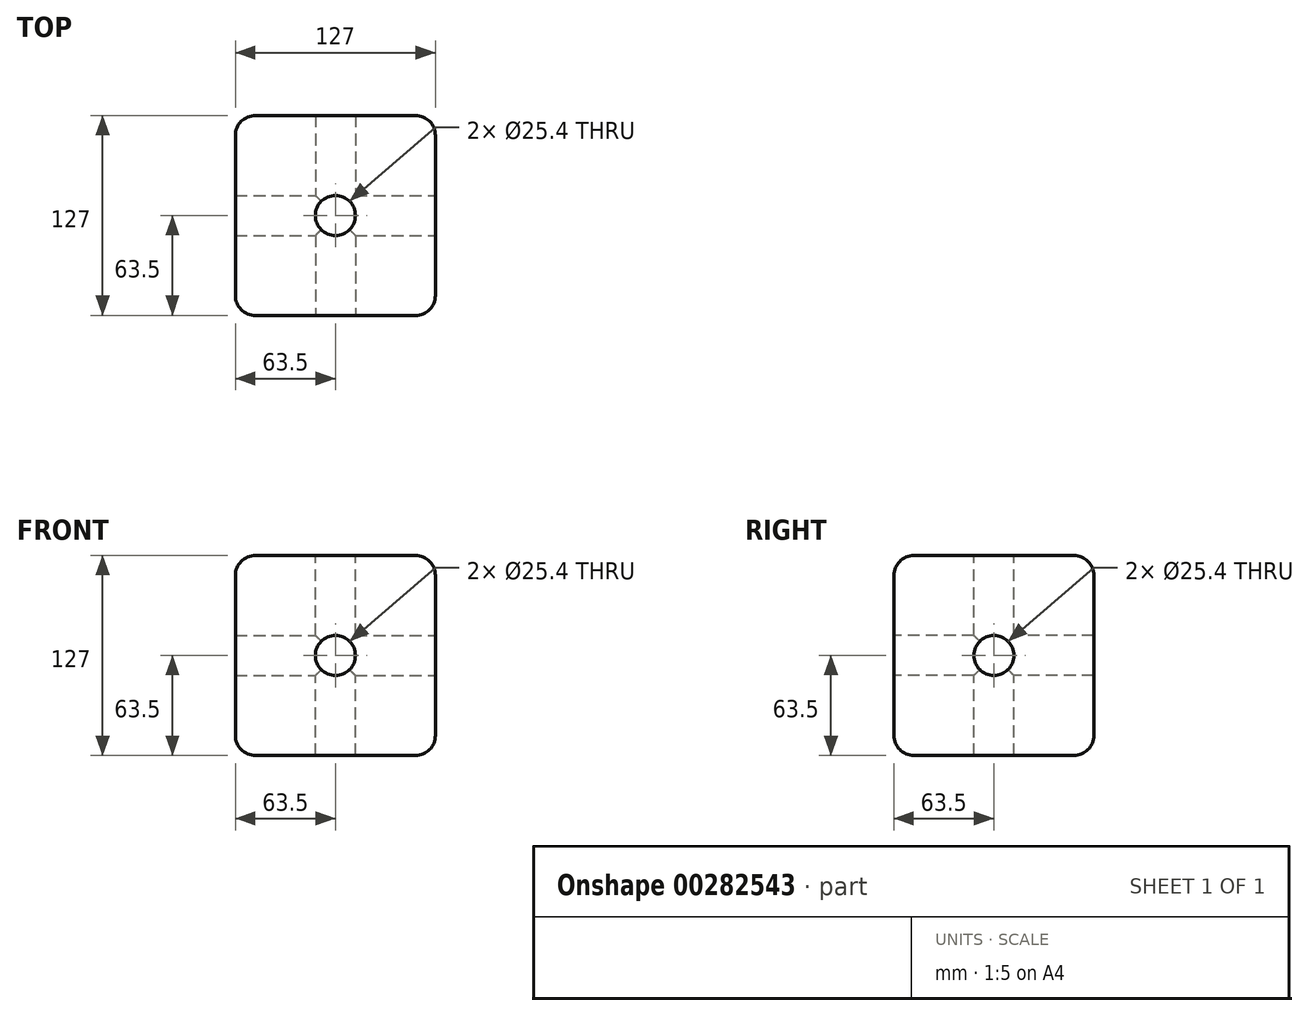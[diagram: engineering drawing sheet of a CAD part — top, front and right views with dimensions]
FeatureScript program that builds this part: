
annotation { "Feature Type Name" : "Feature", "Feature Type Description" : "" }
export const myFeature = defineFeature(function(context is Context, id is Id, definition is map)
    precondition{}
    {
        {
            var Q0;
            Q0=qCreatedBy(makeId("Top.planeOp"),FACE);
            var sketch = newSketch(context, id + "F0", { "sketchPlane" : qUnion([Q0])});
            skLineSegment(sketch, "E0.bottom", {"start": v(63.5, 63.5) * mm, "end": v(-63.5, 63.5) * mm});
            skLineSegment(sketch, "E0.top", {"start": v(63.5, -63.5) * mm, "end": v(-63.5, -63.5) * mm});
            skLineSegment(sketch, "E0.left", {"start": v(63.5, 63.5) * mm, "end": v(63.5, -63.5) * mm});
            skLineSegment(sketch, "E0.right", {"start": v(-63.5, 63.5) * mm, "end": v(-63.5, -63.5) * mm});
            skPoint(sketch, "E0.middle", {"position": v(0, 0) * mm});
            skSolve(sketch);
        }
        {
            var Q0;
            Q0=makeQuery(id+"F0.imprint","IMPRINT",FACE,{"disambiguationData":[TD([[makeQuery(id+"F0.imprint","IMPRINT",EDGE,{"derivedFrom":sQuery(id+"F0.wireOp",EDGE,"E0.bottom")}),1.0]])]});
            extrude(context, id + "F1", {"entities" : qUnion([Q0]), "depth" : 63.5 * mm});
        }
        {
            var Q0;
            Q0=makeQuery(id+"F1.opExtrude","CAP_FACE",FACE,{"disambiguationData":[OSD([sQuery(id+"F0.wireOp",EDGE,"E0.bottom"),sQuery(id+"F0.wireOp",EDGE,"E0.top"),sQuery(id+"F0.wireOp",EDGE,"E0.left"),sQuery(id+"F0.wireOp",EDGE,"E0.right")])],"isStart":true});
            var Q1;
            Q1=makeQuery(id+"F1.opExtrude","CAP_FACE",FACE,{"disambiguationData":[OSD([sQuery(id+"F0.wireOp",EDGE,"E0.bottom"),sQuery(id+"F0.wireOp",EDGE,"E0.top"),sQuery(id+"F0.wireOp",EDGE,"E0.left"),sQuery(id+"F0.wireOp",EDGE,"E0.right")])],"isStart":false});
            extrude(context, id + "F2", {"entities" : qUnion([Q0, Q1]), "operationType" : NewBodyOperationType.ADD, "depth" : 63.5 * mm});
        }
        {
            var Q0;
            Q0=makeQuery(id+"F1.opExtrude","CAP_EDGE",EDGE,{"disambiguationData":[OSD([sQuery(id+"F0.wireOp",EDGE,"E0.top")])],"isStart":false});
            var Q1;
            Q1=makeQuery(id+"F1.opExtrude","CAP_EDGE",EDGE,{"disambiguationData":[OSD([sQuery(id+"F0.wireOp",EDGE,"E0.right")])],"isStart":false});
            var Q2;
            {var subQ0=sQuery(id+"F0.wireOp",EDGE,"E0.right");var subQ1=sQuery(id+"F0.wireOp",EDGE,"E0.top");Q2=makeQuery(id+"F2.boolean.opBoolean","MERGE",EDGE,{"derivedFrom":[makeQuery(id+"F1.opExtrude","SWEPT_EDGE",EDGE,{"disambiguationData":[OSD([subQ1,subQ0])]}),makeQuery(id+"F2.opExtrude","SWEPT_EDGE",EDGE,{"disambiguationData":[OSD([subQ1,subQ0]),TDD([makeQuery(id+"F1.opExtrude","CAP_VERTEX",VERTEX,{"disambiguationData":[OSD([subQ1,subQ0])],"isStart":true})])]}),makeQuery(id+"F2.opExtrude","SWEPT_EDGE",EDGE,{"disambiguationData":[OSD([subQ1,subQ0]),TDD([makeQuery(id+"F1.opExtrude","CAP_VERTEX",VERTEX,{"disambiguationData":[OSD([subQ1,subQ0])],"isStart":false})])]})]});}
            var Q3;
            Q3=makeQuery(id+"F1.opExtrude","CAP_EDGE",EDGE,{"disambiguationData":[OSD([sQuery(id+"F0.wireOp",EDGE,"E0.bottom")])],"isStart":false});
            var Q4;
            Q4=makeQuery(id+"F1.opExtrude","CAP_EDGE",EDGE,{"disambiguationData":[OSD([sQuery(id+"F0.wireOp",EDGE,"E0.left")])],"isStart":false});
            var Q5;
            {var subQ0=sQuery(id+"F0.wireOp",EDGE,"E0.left");var subQ1=sQuery(id+"F0.wireOp",EDGE,"E0.bottom");Q5=makeQuery(id+"F2.boolean.opBoolean","MERGE",EDGE,{"derivedFrom":[makeQuery(id+"F1.opExtrude","SWEPT_EDGE",EDGE,{"disambiguationData":[OSD([subQ1,subQ0])]}),makeQuery(id+"F2.opExtrude","SWEPT_EDGE",EDGE,{"disambiguationData":[OSD([subQ1,subQ0]),TDD([makeQuery(id+"F1.opExtrude","CAP_VERTEX",VERTEX,{"disambiguationData":[OSD([subQ1,subQ0])],"isStart":true})])]}),makeQuery(id+"F2.opExtrude","SWEPT_EDGE",EDGE,{"disambiguationData":[OSD([subQ1,subQ0]),TDD([makeQuery(id+"F1.opExtrude","CAP_VERTEX",VERTEX,{"disambiguationData":[OSD([subQ1,subQ0])],"isStart":false})])]})]});}
            var Q6;
            {var subQ0=sQuery(id+"F0.wireOp",EDGE,"E0.left");var subQ1=sQuery(id+"F0.wireOp",EDGE,"E0.top");Q6=makeQuery(id+"F2.boolean.opBoolean","MERGE",EDGE,{"derivedFrom":[makeQuery(id+"F1.opExtrude","SWEPT_EDGE",EDGE,{"disambiguationData":[OSD([subQ1,subQ0])]}),makeQuery(id+"F2.opExtrude","SWEPT_EDGE",EDGE,{"disambiguationData":[OSD([subQ1,subQ0]),TDD([makeQuery(id+"F1.opExtrude","CAP_VERTEX",VERTEX,{"disambiguationData":[OSD([subQ1,subQ0])],"isStart":true})])]}),makeQuery(id+"F2.opExtrude","SWEPT_EDGE",EDGE,{"disambiguationData":[OSD([subQ1,subQ0]),TDD([makeQuery(id+"F1.opExtrude","CAP_VERTEX",VERTEX,{"disambiguationData":[OSD([subQ1,subQ0])],"isStart":false})])]})]});}
            var Q7;
            {var subQ0=sQuery(id+"F0.wireOp",EDGE,"E0.left");Q7=makeQuery(id+"F2.opExtrude","CAP_EDGE",EDGE,{"disambiguationData":[OSD([subQ0]),TDD([makeQuery(id+"F1.opExtrude","CAP_EDGE",EDGE,{"disambiguationData":[OSD([subQ0])],"isStart":true})])],"isStart":false});}
            var Q8;
            {var subQ0=sQuery(id+"F0.wireOp",EDGE,"E0.top");Q8=makeQuery(id+"F2.opExtrude","CAP_EDGE",EDGE,{"disambiguationData":[OSD([subQ0]),TDD([makeQuery(id+"F1.opExtrude","CAP_EDGE",EDGE,{"disambiguationData":[OSD([subQ0])],"isStart":true})])],"isStart":false});}
            var Q9;
            {var subQ0=sQuery(id+"F0.wireOp",EDGE,"E0.right");var subQ1=sQuery(id+"F0.wireOp",EDGE,"E0.bottom");Q9=makeQuery(id+"F2.boolean.opBoolean","MERGE",EDGE,{"derivedFrom":[makeQuery(id+"F1.opExtrude","SWEPT_EDGE",EDGE,{"disambiguationData":[OSD([subQ1,subQ0])]}),makeQuery(id+"F2.opExtrude","SWEPT_EDGE",EDGE,{"disambiguationData":[OSD([subQ1,subQ0]),TDD([makeQuery(id+"F1.opExtrude","CAP_VERTEX",VERTEX,{"disambiguationData":[OSD([subQ1,subQ0])],"isStart":true})])]}),makeQuery(id+"F2.opExtrude","SWEPT_EDGE",EDGE,{"disambiguationData":[OSD([subQ1,subQ0]),TDD([makeQuery(id+"F1.opExtrude","CAP_VERTEX",VERTEX,{"disambiguationData":[OSD([subQ1,subQ0])],"isStart":false})])]})]});}
            var Q10;
            {var subQ0=sQuery(id+"F0.wireOp",EDGE,"E0.bottom");Q10=makeQuery(id+"F2.opExtrude","CAP_EDGE",EDGE,{"disambiguationData":[OSD([subQ0]),TDD([makeQuery(id+"F1.opExtrude","CAP_EDGE",EDGE,{"disambiguationData":[OSD([subQ0])],"isStart":true})])],"isStart":false});}
            var Q11;
            {var subQ0=sQuery(id+"F0.wireOp",EDGE,"E0.right");Q11=makeQuery(id+"F2.opExtrude","CAP_EDGE",EDGE,{"disambiguationData":[OSD([subQ0]),TDD([makeQuery(id+"F1.opExtrude","CAP_EDGE",EDGE,{"disambiguationData":[OSD([subQ0])],"isStart":true})])],"isStart":false});}
            fillet(context, id + "F3", {"entities" : qUnion([Q0, Q1, Q2, Q3, Q4, Q5, Q6, Q7, Q8, Q9, Q10, Q11]), "radius" : 12.7 * mm, "tangentPropagation" : true, "allowEdgeOverflow" : false});
        }
        {
            var Q0;
            Q0=makeQuery(id+"F1.opExtrude","CAP_FACE",FACE,{"disambiguationData":[OSD([sQuery(id+"F0.wireOp",EDGE,"E0.bottom"),sQuery(id+"F0.wireOp",EDGE,"E0.top"),sQuery(id+"F0.wireOp",EDGE,"E0.left"),sQuery(id+"F0.wireOp",EDGE,"E0.right")])],"isStart":false});
            var sketch = newSketch(context, id + "F4", { "sketchPlane" : qUnion([Q0])});
            skCircle(sketch, "E1", {"center": v(0, 0) * mm, "radius": 12.7 * mm});
            skSolve(sketch);
        }
        {
            var Q0;
            Q0=makeQuery(id+"F4.imprint","IMPRINT",FACE,{"disambiguationData":[TD([[makeQuery(id+"F4.imprint","IMPRINT",EDGE,{"derivedFrom":sQuery(id+"F4.wireOp",EDGE,"E1")}),1.0]])]});
            extrude(context, id + "F5", {"entities" : qUnion([Q0]), "operationType" : NewBodyOperationType.REMOVE, "oppositeDirection" : true, "depth" : 127 * mm});
        }
        {
            var Q0;
            {var subQ0=sQuery(id+"F0.wireOp",EDGE,"E0.top");Q0=makeQuery(id+"F2.boolean.opBoolean","MERGE",FACE,{"derivedFrom":[makeQuery(id+"F1.opExtrude","SWEPT_FACE",FACE,{"disambiguationData":[OSD([subQ0])]}),makeQuery(id+"F2.opExtrude","SWEPT_FACE",FACE,{"disambiguationData":[OSD([subQ0]),TDD([makeQuery(id+"F1.opExtrude","CAP_EDGE",EDGE,{"disambiguationData":[OSD([subQ0])],"isStart":true})])]}),makeQuery(id+"F2.opExtrude","SWEPT_FACE",FACE,{"disambiguationData":[OSD([subQ0]),TDD([makeQuery(id+"F1.opExtrude","CAP_EDGE",EDGE,{"disambiguationData":[OSD([subQ0])],"isStart":false})])]})]});}
            var sketch = newSketch(context, id + "F6", { "sketchPlane" : qUnion([Q0])});
            skCircle(sketch, "E2", {"center": v(0, 0) * mm, "radius": 12.7 * mm});
            skSolve(sketch);
        }
        {
            var Q0;
            Q0=makeQuery(id+"F6.imprint","IMPRINT",FACE,{"disambiguationData":[TD([[makeQuery(id+"F6.imprint","IMPRINT",EDGE,{"derivedFrom":sQuery(id+"F6.wireOp",EDGE,"E2")}),1.0]])]});
            extrude(context, id + "F7", {"entities" : qUnion([Q0]), "operationType" : NewBodyOperationType.REMOVE, "oppositeDirection" : true, "depth" : 127 * mm});
        }
        {
            var Q0;
            {var subQ0=sQuery(id+"F0.wireOp",EDGE,"E0.left");Q0=makeQuery(id+"F2.boolean.opBoolean","MERGE",FACE,{"derivedFrom":[makeQuery(id+"F1.opExtrude","SWEPT_FACE",FACE,{"disambiguationData":[OSD([subQ0])]}),makeQuery(id+"F2.opExtrude","SWEPT_FACE",FACE,{"disambiguationData":[OSD([subQ0]),TDD([makeQuery(id+"F1.opExtrude","CAP_EDGE",EDGE,{"disambiguationData":[OSD([subQ0])],"isStart":true})])]}),makeQuery(id+"F2.opExtrude","SWEPT_FACE",FACE,{"disambiguationData":[OSD([subQ0]),TDD([makeQuery(id+"F1.opExtrude","CAP_EDGE",EDGE,{"disambiguationData":[OSD([subQ0])],"isStart":false})])]})]});}
            var sketch = newSketch(context, id + "F8", { "sketchPlane" : qUnion([Q0])});
            skCircle(sketch, "E3", {"center": v(0, 0) * mm, "radius": 12.7 * mm});
            skSolve(sketch);
        }
        {
            var Q0;
            Q0=makeQuery(id+"F8.imprint","IMPRINT",FACE,{"disambiguationData":[TD([[makeQuery(id+"F8.imprint","IMPRINT",EDGE,{"derivedFrom":sQuery(id+"F8.wireOp",EDGE,"E3")}),1.0]])]});
            extrude(context, id + "F9", {"entities" : qUnion([Q0]), "operationType" : NewBodyOperationType.REMOVE, "oppositeDirection" : true, "depth" : 381 * mm});
        }
    });
